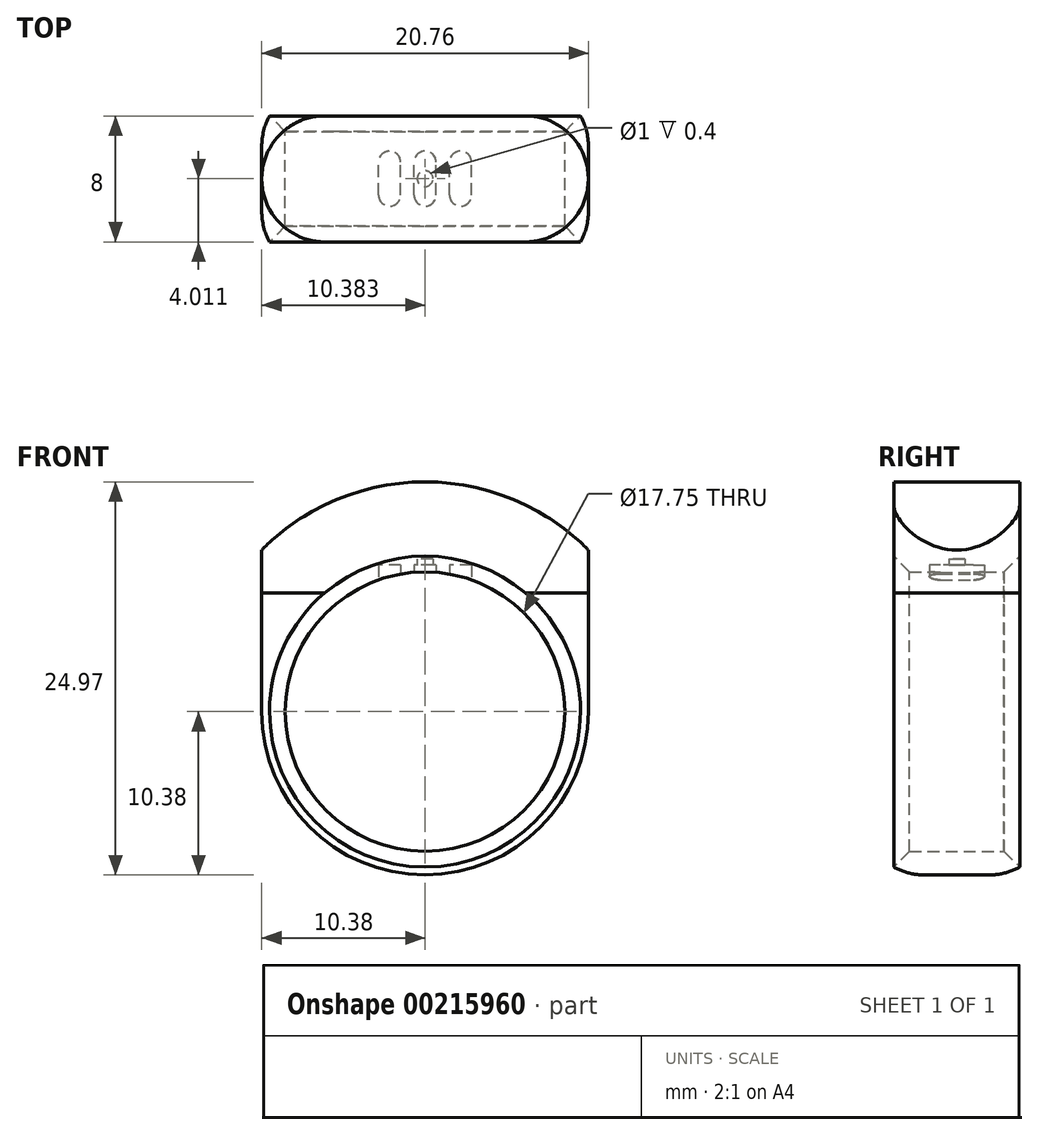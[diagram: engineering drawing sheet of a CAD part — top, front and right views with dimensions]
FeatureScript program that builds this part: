
annotation { "Feature Type Name" : "Feature", "Feature Type Description" : "" }
export const myFeature = defineFeature(function(context is Context, id is Id, definition is map)
    precondition{}
    {
        {
            var Q0;
            Q0=qCreatedBy(makeId("Front.planeOp"),FACE);
            var sketch = newSketch(context, id + "F0", { "sketchPlane" : qUnion([Q0])});
            skCircle(sketch, "E0", {"center": v(0, 0) * mm, "radius": 8.88 * mm});
            skCircle(sketch, "E1.0", {"center": v(0, 0) * mm, "radius": 10.38 * mm});
            skCircle(sketch, "E2.0", {"center": v(0, 0) * mm, "radius": 20.38 * mm});
            skLineSegment(sketch, "E3", {"start": v(10.38, 0) * mm, "end": v(10.38, 17.54) * mm});
            skLineSegment(sketch, "E4.MirrorCS", {"start": v(-10.38, 0) * mm, "end": v(-10.38, 17.54) * mm});
            skCircle(sketch, "E5.0", {"center": v(0, 0) * mm, "radius": 19.38 * mm});
            skLineSegment(sketch, "E6", {"start": v(-0.5, 20.37) * mm, "end": v(-0.5, 19.37) * mm});
            skLineSegment(sketch, "E7.MirrorCS", {"start": v(0.5, 20.37) * mm, "end": v(0.5, 19.37) * mm});
            skLineSegment(sketch, "E8", {"start": v(0, 20.38) * mm, "end": v(0, 19.38) * mm});
            skArc(sketch, "E9", {"start": v(10.37, 10.26) * mm, "mid": v(0, 14.6) * mm, "end": v(-10.38, 10.26) * mm});
            skLineSegment(sketch, "E10", {"start": v(0, 19.38) * mm, "end": v(0, 14.6) * mm});
            skSolve(sketch);
        }
        {
            var Q0;
            Q0=makeQuery(id+"F0.imprint","IMPRINT",FACE,{"disambiguationData":[TD([[makeQuery(id+"F0.imprint","IMPRINT",EDGE,{"derivedFrom":sQuery(id+"F0.wireOp",EDGE,"E0")}),-1.0]])]});
            extrude(context, id + "F1", {"entities" : qUnion([Q0]), "depth" : 4 * mm, "hasSecondDirection" : true, "secondDirectionOppositeDirection" : true, "secondDirectionDepth" : 4 * mm});
        }
        {
            var Q0;
            Q0=makeQuery(id+"F1.opExtrude","CAP_EDGE",EDGE,{"disambiguationData":[OSD([sQuery(id+"F0.wireOp",EDGE,"E0")])],"isStart":false});
            var Q1;
            Q1=makeQuery(id+"F1.opExtrude","CAP_EDGE",EDGE,{"disambiguationData":[OSD([sQuery(id+"F0.wireOp",EDGE,"E0")])],"isStart":true});
            chamfer(context, id + "F2", {"entities" : qUnion([Q0, Q1]), "width" : 1 * mm, "tangentPropagation" : true});
        }
        {
            var Q0;
            {var subQ0=sQuery(id+"F0.wireOp",EDGE,"E3");var subQ1=sQuery(id+"F0.wireOp",EDGE,"E1.0");var subQ2=makeQuery(id+"F0.imprint","INTERSECT",VERTEX,{"derivedFrom":[subQ1,subQ0]});Q0=makeQuery(id+"F0.imprint","IMPRINT",FACE,{"disambiguationData":[TD([[makeQuery(id+"F0.imprint","IMPRINT",EDGE,{"disambiguationData":[TD([[subQ2,-1.0]])],"derivedFrom":subQ1}),-1.0]])]});}
            extrude(context, id + "F3", {"entities" : qUnion([Q0]), "operationType" : NewBodyOperationType.ADD, "depth" : 4 * mm, "hasSecondDirection" : true, "secondDirectionOppositeDirection" : true, "secondDirectionDepth" : 4 * mm});
        }
        {
            var Q0;
            Q0=makeQuery(id+"F3.opExtrude","CAP_EDGE",EDGE,{"disambiguationData":[OSD([sQuery(id+"F0.wireOp",EDGE,"E3")])],"isStart":false});
            var Q1;
            Q1=makeQuery(id+"F3.opExtrude","CAP_EDGE",EDGE,{"disambiguationData":[OSD([sQuery(id+"F0.wireOp",EDGE,"E3")])],"isStart":true});
            var Q2;
            Q2=makeQuery(id+"F3.opExtrude","CAP_EDGE",EDGE,{"disambiguationData":[OSD([sQuery(id+"F0.wireOp",EDGE,"E4.MirrorCS")])],"isStart":false});
            var Q3;
            Q3=makeQuery(id+"F3.opExtrude","CAP_EDGE",EDGE,{"disambiguationData":[OSD([sQuery(id+"F0.wireOp",EDGE,"E4.MirrorCS")])],"isStart":true});
            fillet(context, id + "F4", {"entities" : qUnion([Q0, Q1, Q2, Q3]), "radius" : 4 * mm, "tangentPropagation" : true, "allowEdgeOverflow" : false});
        }
        {
            var Q0;
            Q0=qCreatedBy(makeId("Top.planeOp"),FACE);
            var sketch = newSketch(context, id + "F5", { "sketchPlane" : qUnion([Q0])});
            skLineSegment(sketch, "E11.bottom", {"start": v(-0.7, 1.06) * mm, "end": v(-0.7, -1.03) * mm});
            skArc(sketch, "E12.filletArc", {"start": v(0.7, 1.06) * mm, "mid": v(0.5, 1.56) * mm, "end": v(0, 1.76) * mm});
            skArc(sketch, "E13.filletArc", {"start": v(0, 1.76) * mm, "mid": v(-0.49, 1.56) * mm, "end": v(-0.7, 1.06) * mm});
            skArc(sketch, "E14.filletArc", {"start": v(0, -1.73) * mm, "mid": v(0.5, -1.52) * mm, "end": v(0.7, -1.03) * mm});
            skArc(sketch, "E15.filletArc", {"start": v(-0.7, -1.03) * mm, "mid": v(-0.49, -1.52) * mm, "end": v(0, -1.73) * mm});
            skLineSegment(sketch, "E16.bottom", {"start": v(-2.95, 1.06) * mm, "end": v(-2.95, -1.03) * mm});
            skLineSegment(sketch, "E16.top", {"start": v(-1.55, 1.06) * mm, "end": v(-1.55, -1.03) * mm});
            skArc(sketch, "E17.filletArc", {"start": v(-1.55, 1.06) * mm, "mid": v(-1.75, 1.56) * mm, "end": v(-2.25, 1.76) * mm});
            skArc(sketch, "E18.filletArc", {"start": v(-2.25, 1.76) * mm, "mid": v(-2.74, 1.56) * mm, "end": v(-2.95, 1.06) * mm});
            skArc(sketch, "E19.filletArc", {"start": v(-2.25, -1.73) * mm, "mid": v(-1.75, -1.52) * mm, "end": v(-1.55, -1.03) * mm});
            skArc(sketch, "E20.filletArc", {"start": v(-2.95, -1.03) * mm, "mid": v(-2.74, -1.52) * mm, "end": v(-2.25, -1.73) * mm});
            skLineSegment(sketch, "E21", {"start": v(0.7, 1.06) * mm, "end": v(0.7, -1.03) * mm});
            skCircle(sketch, "E22", {"center": v(0, 0.01) * mm, "radius": 0.5 * mm});
            skLineSegment(sketch, "E23.bottom", {"start": v(1.56, 1.06) * mm, "end": v(1.56, -1.03) * mm});
            skLineSegment(sketch, "E23.top", {"start": v(2.96, 1.06) * mm, "end": v(2.96, -1.03) * mm});
            skArc(sketch, "E24.filletArc", {"start": v(2.96, 1.06) * mm, "mid": v(2.75, 1.56) * mm, "end": v(2.26, 1.76) * mm});
            skArc(sketch, "E25.filletArc", {"start": v(2.26, 1.76) * mm, "mid": v(1.76, 1.56) * mm, "end": v(1.56, 1.06) * mm});
            skArc(sketch, "E26.filletArc", {"start": v(2.26, -1.73) * mm, "mid": v(2.75, -1.52) * mm, "end": v(2.96, -1.03) * mm});
            skArc(sketch, "E27.filletArc", {"start": v(1.56, -1.03) * mm, "mid": v(1.76, -1.52) * mm, "end": v(2.26, -1.73) * mm});
            skSolve(sketch);
        }
        {
            var Q0;
            Q0=makeQuery(id+"F5.imprint","IMPRINT",FACE,{"disambiguationData":[TD([[makeQuery(id+"F5.imprint","IMPRINT",EDGE,{"derivedFrom":sQuery(id+"F5.wireOp",EDGE,"E23.bottom")}),1.0]])]});
            var Q1;
            Q1=makeQuery(id+"F5.imprint","IMPRINT",FACE,{"disambiguationData":[TD([[makeQuery(id+"F5.imprint","IMPRINT",EDGE,{"derivedFrom":sQuery(id+"F5.wireOp",EDGE,"E11.bottom")}),1.0]])]});
            var Q2;
            Q2=makeQuery(id+"F5.imprint","IMPRINT",FACE,{"disambiguationData":[TD([[makeQuery(id+"F5.imprint","IMPRINT",EDGE,{"derivedFrom":sQuery(id+"F5.wireOp",EDGE,"E16.bottom")}),1.0]])]});
            extrude(context, id + "F6", {"entities" : qUnion([Q0, Q1, Q2]), "operationType" : NewBodyOperationType.REMOVE, "depth" : 9.3 * mm, "offsetDistance" : 25 * mm});
        }
        {
            var Q0;
            Q0=makeQuery(id+"F5.imprint","IMPRINT",FACE,{"disambiguationData":[TD([[makeQuery(id+"F5.imprint","IMPRINT",EDGE,{"derivedFrom":sQuery(id+"F5.wireOp",EDGE,"E22")}),1.0]])]});
            extrude(context, id + "F7", {"entities" : qUnion([Q0]), "operationType" : NewBodyOperationType.REMOVE, "depth" : 9.7 * mm, "offsetDistance" : 25 * mm});
        }
    });
